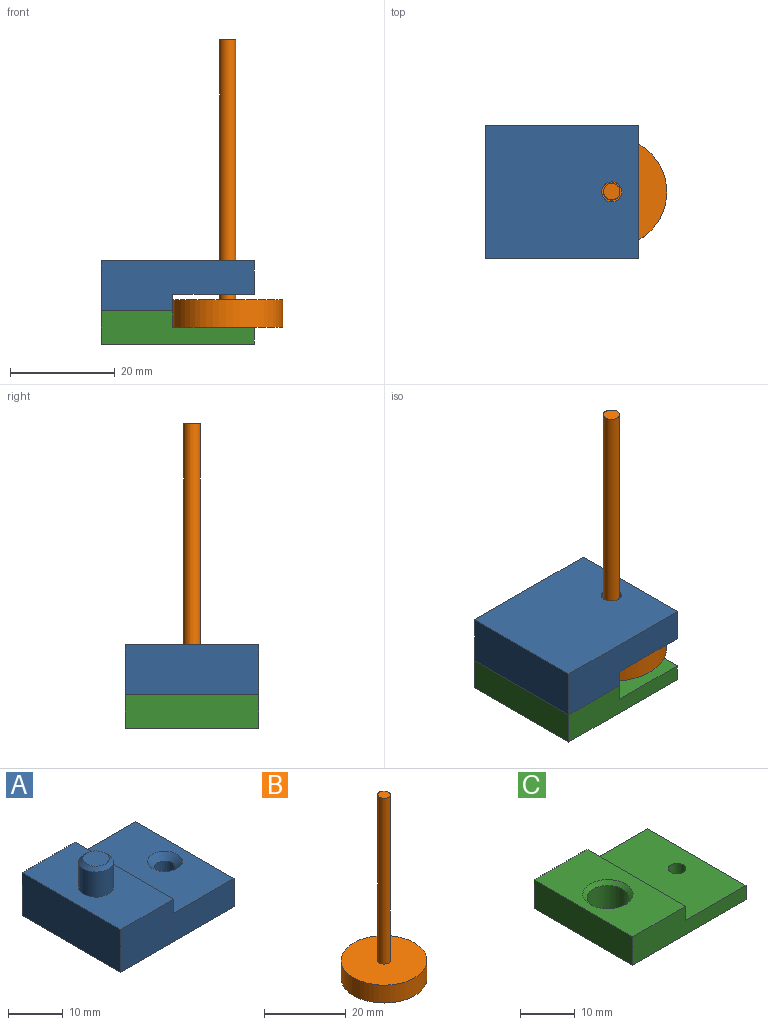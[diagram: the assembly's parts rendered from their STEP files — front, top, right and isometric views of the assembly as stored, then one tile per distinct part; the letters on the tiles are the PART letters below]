
ASSEMBLY  parts=3 mates=2
PART A: 13 faces, bbox 29.2x25.4x15.9 mm
  f0: plane 25.4x15.56mm, normal (0,0,1), area 363.5mm2, adj f2,f3,f4,f7,f12
  f1: plane 25.4x9.53mm, normal (-1,0,0), area 241.9mm2, adj f2,f4,f6,f8
  f2: plane 29.21x9.53mm, normal (0,-1,0), area 228.8mm2, adj f0,f1,f3,f6,f7,f8
  f3: plane 25.4x6.35mm, normal (1,0,0), area 161.3mm2, adj f0,f2,f4,f6
  f4: plane 29.21x9.53mm, normal (0,1,0), area 228.8mm2, adj f0,f1,f3,f6,f7,f8
  f5: cylinder r=1.91mm len=5.08mm, axis (0,0,-1), area 60.8mm2, adj f6,f12
  f6: plane 29.21x25.4mm, normal (0,0,-1), area 730.5mm2, adj f1,f2,f3,f4,f5
  f7: plane 25.4x3.18mm, normal (1,0,0), area 80.6mm2, adj f0,f2,f4,f8
  f8: plane 25.4x13.65mm, normal (0,0,1), area 315.1mm2, adj f1,f2,f4,f7,f10
  f9: plane 4.83x4.83mm, normal (0,0,1), area 18.3mm2, adj f11
  f10: cylinder r=3.17mm len=6.35mm, axis (0,0,-1), area 111.5mm2, adj f8,f11
  f11: cone r=2.41mm half-angle=45deg, axis (0,0,-1), area 18.9mm2, adj f9,f10
  f12: cone r=1.91mm half-angle=45deg, axis (0,0,1), area 28.7mm2, adj f0,f5
PART B: 5 faces, bbox 21x21x54.9 mm
  f0: cylinder r=10.48mm len=20.96mm, axis (0,0,-1), area 351.1mm2, adj f1,f2
  f1: plane 20.96x20.96mm, normal (0,0,1), area 337.2mm2, adj f0,f3
  f2: plane 20.96x20.96mm, normal (0,0,-1), area 344.9mm2, adj f0
  f3: cylinder r=1.56mm len=49.53mm, axis (0,0,-1), area 486.1mm2, adj f1,f4
  f4: plane 3.12x3.12mm, normal (0,0,1), area 7.7mm2, adj f3
PART C: 11 faces, bbox 29.2x25.4x6.4 mm
  f0: plane 25.4x15.56mm, normal (0,0,1), area 386.9mm2, adj f1,f2,f7,f9,f10
  f1: plane 29.21x6.35mm, normal (0,1,0), area 136.1mm2, adj f0,f3,f5,f6,f7,f9
  f2: plane 29.21x6.35mm, normal (0,-1,0), area 136.1mm2, adj f0,f3,f5,f6,f7,f9
  f3: plane 25.4x6.35mm, normal (-1,0,0), area 161.3mm2, adj f1,f2,f5,f6
  f4: cylinder r=3.81mm len=7.62mm, axis (0,0,-1), area 133.8mm2, adj f6,f8
  f5: plane 25.4x13.65mm, normal (0,0,1), area 281.1mm2, adj f1,f2,f3,f7,f8
  f6: plane 29.21x25.4mm, normal (0,0,-1), area 688mm2, adj f1,f2,f3,f4,f9,f10
  f7: plane 25.4x3.18mm, normal (1,0,0), area 80.6mm2, adj f0,f1,f2,f5
  f8: cone r=3.81mm half-angle=45deg, axis (0,0,1), area 28.4mm2, adj f4,f5
  f9: plane 25.4x3.18mm, normal (1,0,0), area 80.6mm2, adj f0,f1,f2,f6
  f10: cylinder r=1.63mm len=3.25mm, axis (0,0,-1), area 32.4mm2, adj f0,f6
PLACE A rot(axis=(1,0,0),180deg) t=(-23.06,12.52,12.7)mm
PLACE B t=(1.07,-0.18,0)mm
PLACE C t=(1.07,-0.18,-3.18)mm fixed
MATE fastened A.f10 <-> C.f4  axis (0,0,-1) through (-16.71,-0.18,3.18)mm
MATE cylindrical B.f3 <-> A.f5  axis (0,0,1) through (1.07,-0.18,5.33)mm
